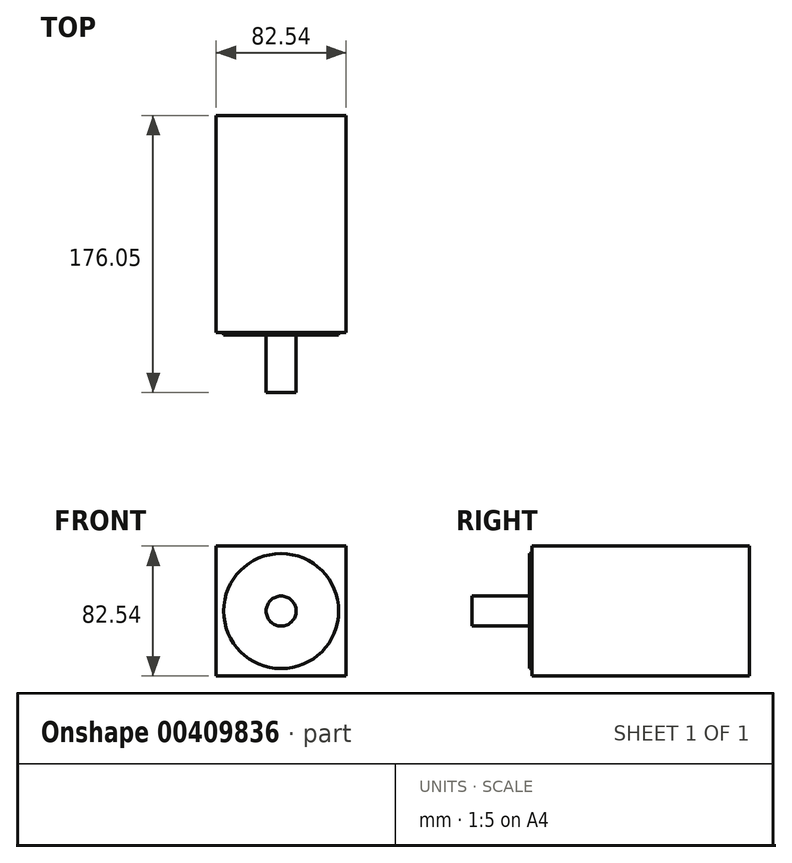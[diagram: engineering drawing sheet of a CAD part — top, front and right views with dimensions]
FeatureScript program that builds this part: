
annotation { "Feature Type Name" : "Feature", "Feature Type Description" : "" }
export const myFeature = defineFeature(function(context is Context, id is Id, definition is map)
    precondition{}
    {
        {
            var Q0;
            Q0=qCreatedBy(makeId("Front.planeOp"),FACE);
            var sketch = newSketch(context, id + "F0", { "sketchPlane" : qUnion([Q0])});
            skLineSegment(sketch, "E0.bottom", {"start": v(-41.28, 41.28) * mm, "end": v(41.28, 41.28) * mm});
            skLineSegment(sketch, "E0.top", {"start": v(-41.27, -41.28) * mm, "end": v(41.28, -41.28) * mm});
            skLineSegment(sketch, "E0.left", {"start": v(-41.28, 41.28) * mm, "end": v(-41.28, -41.28) * mm});
            skLineSegment(sketch, "E0.right", {"start": v(41.28, 41.28) * mm, "end": v(41.28, -41.28) * mm});
            skSolve(sketch);
        }
        {
            var Q0;
            Q0 = qSketchRegion(id + "F0", true);
            extrude(context, id + "F1", {"entities" : qUnion([Q0]), "oppositeDirection" : true, "depth" : 137.95 * mm});
        }
        {
            var Q0;
            Q0=qCreatedBy(makeId("Front.planeOp"),FACE);
            var sketch = newSketch(context, id + "F2", { "sketchPlane" : qUnion([Q0])});
            skCircle(sketch, "E1", {"center": v(0, 0) * mm, "radius": 36.51 * mm});
            skSolve(sketch);
        }
        {
            var Q0;
            Q0 = qSketchRegion(id + "F2", true);
            extrude(context, id + "F3", {"entities" : qUnion([Q0]), "operationType" : NewBodyOperationType.ADD, "depth" : 1.57 * mm});
        }
        {
            var Q0;
            Q0=qCreatedBy(makeId("Front.planeOp"),FACE);
            var sketch = newSketch(context, id + "F4", { "sketchPlane" : qUnion([Q0])});
            skCircle(sketch, "E2", {"center": v(0, 0) * mm, "radius": 9.53 * mm});
            skSolve(sketch);
        }
        {
            var Q0;
            Q0 = qSketchRegion(id + "F4", true);
            extrude(context, id + "F5", {"entities" : qUnion([Q0]), "operationType" : NewBodyOperationType.ADD, "depth" : 38.1 * mm});
        }
    });
